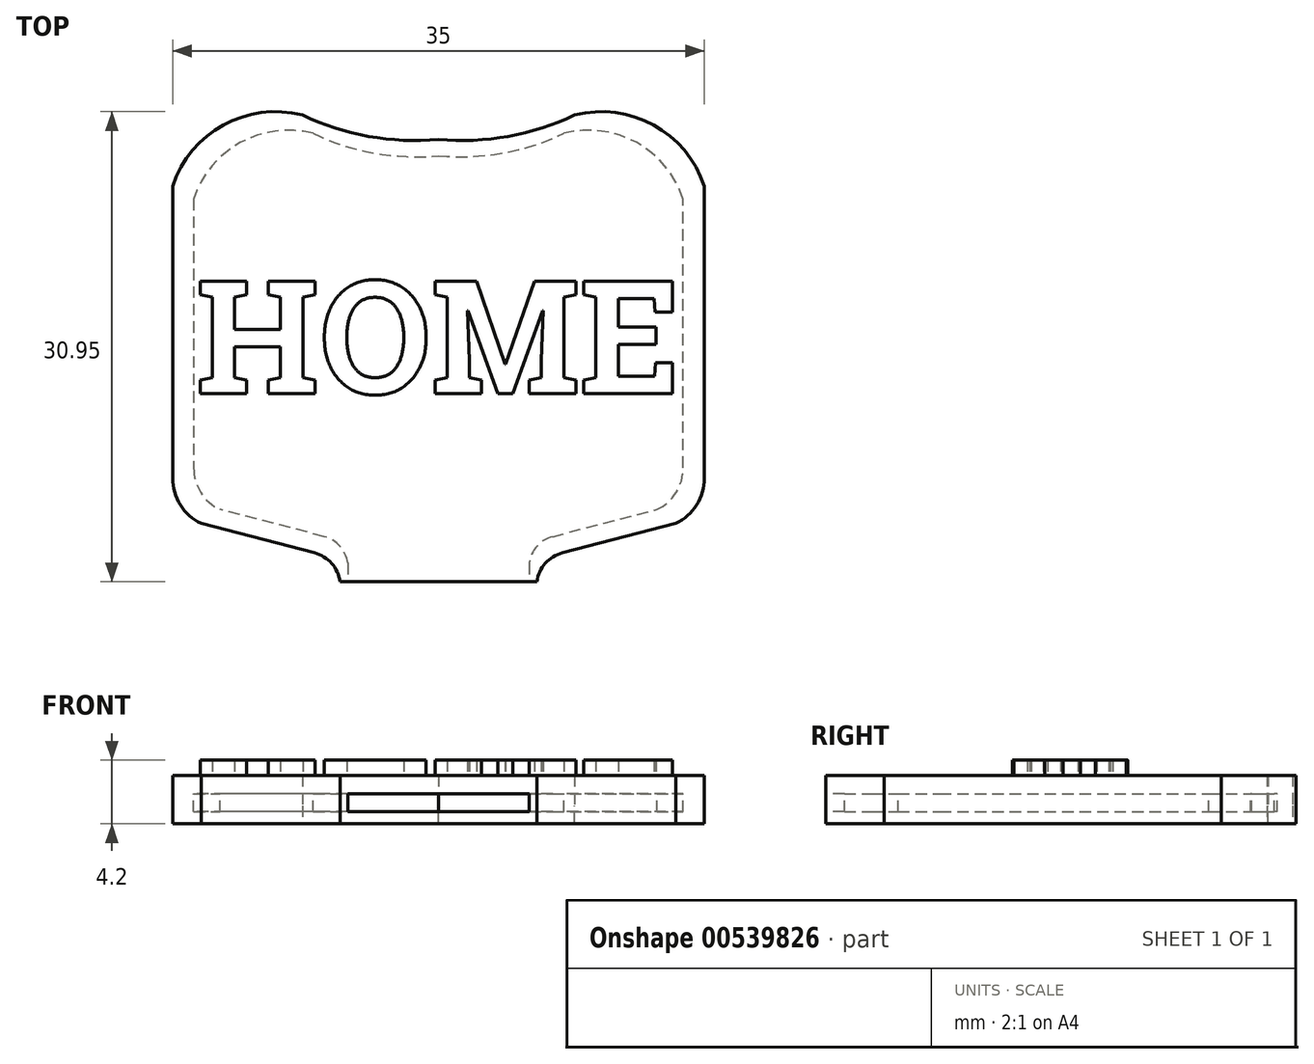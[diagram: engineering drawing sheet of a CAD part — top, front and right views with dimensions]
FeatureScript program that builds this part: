
annotation { "Feature Type Name" : "Feature", "Feature Type Description" : "" }
export const myFeature = defineFeature(function(context is Context, id is Id, definition is map)
    precondition{}
    {
        {
            var Q0;
            Q0=qCreatedBy(makeId("Top.planeOp"),FACE);
            var sketch = newSketch(context, id + "F0", { "sketchPlane" : qUnion([Q0])});
            skArc(sketch, "E0", {"start": v(-27.77, 71.26) * mm, "mid": v(-32.97, 70.6) * mm, "end": v(-36.3, 66.57) * mm});
            skLineSegment(sketch, "E1", {"start": v(-26.97, 42.44) * mm, "end": v(-34.42, 44.37) * mm});
            skArc(sketch, "E2", {"start": v(-36.3, 47.37) * mm, "mid": v(-35.8, 45.6) * mm, "end": v(-34.42, 44.37) * mm});
            skArc(sketch, "E3", {"start": v(-27.77, 71.26) * mm, "mid": v(-23.4, 69.86) * mm, "end": v(-18.8, 69.66) * mm});
            skArc(sketch, "E4", {"start": v(-25.3, 40.54) * mm, "mid": v(-25.85, 41.75) * mm, "end": v(-26.97, 42.44) * mm});
            skArc(sketch, "E5.MirrorCS", {"start": v(-9.85, 71.26) * mm, "mid": v(-14.22, 69.86) * mm, "end": v(-18.8, 69.66) * mm});
            skArc(sketch, "E6.MirrorCS", {"start": v(-9.85, 71.26) * mm, "mid": v(-4.65, 70.6) * mm, "end": v(-1.3, 66.57) * mm});
            skLineSegment(sketch, "E7.MirrorCS", {"start": v(-1.3, 47.37) * mm, "end": v(-1.3, 66.57) * mm});
            skLineSegment(sketch, "E8.MirrorCS", {"start": v(-10.65, 42.44) * mm, "end": v(-3.2, 44.37) * mm});
            skArc(sketch, "E9.MirrorCS", {"start": v(-1.3, 47.37) * mm, "mid": v(-1.82, 45.6) * mm, "end": v(-3.2, 44.37) * mm});
            skArc(sketch, "E10.MirrorCS", {"start": v(-12.32, 40.54) * mm, "mid": v(-11.77, 41.75) * mm, "end": v(-10.65, 42.44) * mm});
            skLineSegment(sketch, "E11", {"start": v(-36.3, 66.57) * mm, "end": v(-36.3, 47.37) * mm});
            skLineSegment(sketch, "E12", {"start": v(-25.3, 40.54) * mm, "end": v(-12.32, 40.54) * mm});
            skSolve(sketch);
        }
        {
            var Q0;
            Q0 = qSketchRegion(id + "F0", true);
            extrude(context, id + "F1", {"entities" : qUnion([Q0]), "depth" : 1.2 * mm, "offsetDistance" : 25.4 * mm});
        }
        {
            var Q0;
            Q0=qCreatedBy(makeId("Top.planeOp"),FACE);
            var sketch = newSketch(context, id + "F2", { "sketchPlane" : qUnion([Q0])});
            skArc(sketch, "E13", {"start": v(-27.77, 71.26) * mm, "mid": v(-32.97, 70.6) * mm, "end": v(-36.3, 66.57) * mm});
            skLineSegment(sketch, "E14", {"start": v(-26.97, 42.44) * mm, "end": v(-34.43, 44.37) * mm});
            skArc(sketch, "E15", {"start": v(-36.3, 47.36) * mm, "mid": v(-35.8, 45.6) * mm, "end": v(-34.43, 44.37) * mm});
            skArc(sketch, "E16", {"start": v(-27.77, 71.26) * mm, "mid": v(-23.4, 69.86) * mm, "end": v(-18.8, 69.66) * mm});
            skArc(sketch, "E17", {"start": v(-25.3, 40.54) * mm, "mid": v(-25.85, 41.75) * mm, "end": v(-26.97, 42.44) * mm});
            skArc(sketch, "E18.MirrorCS", {"start": v(-9.85, 71.26) * mm, "mid": v(-14.22, 69.86) * mm, "end": v(-18.8, 69.66) * mm});
            skArc(sketch, "E19.MirrorCS", {"start": v(-9.85, 71.26) * mm, "mid": v(-4.65, 70.6) * mm, "end": v(-1.3, 66.57) * mm});
            skLineSegment(sketch, "E20.MirrorCS", {"start": v(-1.3, 47.36) * mm, "end": v(-1.3, 66.57) * mm});
            skLineSegment(sketch, "E21.MirrorCS", {"start": v(-10.65, 42.44) * mm, "end": v(-3.2, 44.37) * mm});
            skArc(sketch, "E22.MirrorCS", {"start": v(-1.3, 47.36) * mm, "mid": v(-1.82, 45.6) * mm, "end": v(-3.2, 44.37) * mm});
            skArc(sketch, "E23.MirrorCS", {"start": v(-12.32, 40.54) * mm, "mid": v(-11.77, 41.75) * mm, "end": v(-10.65, 42.44) * mm});
            skLineSegment(sketch, "E24", {"start": v(-36.3, 66.57) * mm, "end": v(-36.3, 47.36) * mm});
            skArc(sketch, "E25", {"start": v(-27.06, 70.05) * mm, "mid": v(-31.85, 69.45) * mm, "end": v(-34.92, 65.73) * mm});
            skLineSegment(sketch, "E26", {"start": v(-26.33, 43.5) * mm, "end": v(-33.19, 45.3) * mm});
            skArc(sketch, "E27", {"start": v(-34.92, 48.05) * mm, "mid": v(-34.45, 46.42) * mm, "end": v(-33.19, 45.3) * mm});
            skArc(sketch, "E28", {"start": v(-27.06, 70.05) * mm, "mid": v(-23.03, 68.76) * mm, "end": v(-18.8, 68.58) * mm});
            skArc(sketch, "E29", {"start": v(-24.78, 41.77) * mm, "mid": v(-25.29, 42.87) * mm, "end": v(-26.33, 43.5) * mm});
            skArc(sketch, "E30.MirrorCS", {"start": v(-10.56, 70.05) * mm, "mid": v(-14.58, 68.76) * mm, "end": v(-18.8, 68.58) * mm});
            skArc(sketch, "E31.MirrorCS", {"start": v(-10.56, 70.05) * mm, "mid": v(-5.77, 69.45) * mm, "end": v(-2.7, 65.73) * mm});
            skLineSegment(sketch, "E32.MirrorCS", {"start": v(-2.7, 48.05) * mm, "end": v(-2.7, 65.73) * mm});
            skLineSegment(sketch, "E33.MirrorCS", {"start": v(-11.3, 43.5) * mm, "end": v(-4.43, 45.3) * mm});
            skArc(sketch, "E34.MirrorCS", {"start": v(-2.7, 48.05) * mm, "mid": v(-3.16, 46.42) * mm, "end": v(-4.43, 45.3) * mm});
            skArc(sketch, "E35.MirrorCS", {"start": v(-12.84, 41.77) * mm, "mid": v(-12.33, 42.87) * mm, "end": v(-11.3, 43.5) * mm});
            skLineSegment(sketch, "E36", {"start": v(-34.92, 65.73) * mm, "end": v(-34.92, 48.05) * mm});
            skLineSegment(sketch, "E37", {"start": v(-25.3, 40.54) * mm, "end": v(-12.32, 40.54) * mm});
            skSolve(sketch);
        }
        {
            var Q0;
            Q0 = qSketchRegion(id + "F2", true);
            extrude(context, id + "F3", {"entities" : qUnion([Q0]), "operationType" : NewBodyOperationType.ADD, "depth" : 2 * mm, "offsetDistance" : 25.4 * mm});
        }
        {
            var Q0;
            Q0=makeQuery(id+"F3.opExtrude","CAP_FACE",FACE,{"disambiguationData":[OSD([sQuery(id+"F2.wireOp",EDGE,"E13"),sQuery(id+"F2.wireOp",EDGE,"E14"),sQuery(id+"F2.wireOp",EDGE,"E15"),sQuery(id+"F2.wireOp",EDGE,"E16"),sQuery(id+"F2.wireOp",EDGE,"E17"),sQuery(id+"F2.wireOp",EDGE,"E18.MirrorCS"),sQuery(id+"F2.wireOp",EDGE,"E19.MirrorCS"),sQuery(id+"F2.wireOp",EDGE,"E20.MirrorCS"),sQuery(id+"F2.wireOp",EDGE,"E21.MirrorCS"),sQuery(id+"F2.wireOp",EDGE,"E22.MirrorCS"),sQuery(id+"F2.wireOp",EDGE,"E23.MirrorCS"),sQuery(id+"F2.wireOp",EDGE,"E24"),sQuery(id+"F2.wireOp",EDGE,"E37")])],"isStart":false});
            var sketch = newSketch(context, id + "F4", { "sketchPlane" : qUnion([Q0])});
            skArc(sketch, "E38", {"start": v(-27.06, 70.06) * mm, "mid": v(-31.85, 69.45) * mm, "end": v(-34.92, 65.74) * mm});
            skLineSegment(sketch, "E39", {"start": v(-26.33, 43.51) * mm, "end": v(-33.19, 45.3) * mm});
            skArc(sketch, "E40", {"start": v(-34.92, 48.05) * mm, "mid": v(-34.45, 46.42) * mm, "end": v(-33.19, 45.3) * mm});
            skArc(sketch, "E41", {"start": v(-27.06, 70.06) * mm, "mid": v(-23.04, 68.77) * mm, "end": v(-18.8, 68.58) * mm});
            skArc(sketch, "E42", {"start": v(-24.78, 41.77) * mm, "mid": v(-25.29, 42.87) * mm, "end": v(-26.33, 43.51) * mm});
            skArc(sketch, "E43.MirrorCS", {"start": v(-10.56, 70.06) * mm, "mid": v(-14.58, 68.77) * mm, "end": v(-18.8, 68.58) * mm});
            skArc(sketch, "E44.MirrorCS", {"start": v(-10.56, 70.06) * mm, "mid": v(-5.77, 69.45) * mm, "end": v(-2.7, 65.74) * mm});
            skLineSegment(sketch, "E45.MirrorCS", {"start": v(-2.7, 48.05) * mm, "end": v(-2.7, 65.74) * mm});
            skLineSegment(sketch, "E46.MirrorCS", {"start": v(-11.3, 43.51) * mm, "end": v(-4.43, 45.3) * mm});
            skArc(sketch, "E47.MirrorCS", {"start": v(-2.7, 48.05) * mm, "mid": v(-3.16, 46.42) * mm, "end": v(-4.43, 45.3) * mm});
            skArc(sketch, "E48.MirrorCS", {"start": v(-12.84, 41.77) * mm, "mid": v(-12.33, 42.87) * mm, "end": v(-11.3, 43.51) * mm});
            skLineSegment(sketch, "E49", {"start": v(-34.92, 65.74) * mm, "end": v(-34.92, 48.05) * mm});
            skLineSegment(sketch, "E50", {"start": v(-24.78, 41.77) * mm, "end": v(-24.78, 40.54) * mm});
            skLineSegment(sketch, "E51", {"start": v(-12.84, 41.77) * mm, "end": v(-12.84, 40.54) * mm});
            skLineSegment(sketch, "E52", {"start": v(-12.84, 40.54) * mm, "end": v(-24.78, 40.54) * mm});
            skSolve(sketch);
        }
        {
            var Q0;
            Q0 = qSketchRegion(id + "F4", true);
            extrude(context, id + "F5", {"entities" : qUnion([Q0]), "operationType" : NewBodyOperationType.REMOVE, "oppositeDirection" : true, "depth" : 1.2 * mm, "offsetDistance" : 25.4 * mm});
        }
        {
            var Q0;
            Q0=makeQuery(id+"F3.opExtrude","CAP_FACE",FACE,{"disambiguationData":[OSD([sQuery(id+"F2.wireOp",EDGE,"E13"),sQuery(id+"F2.wireOp",EDGE,"E14"),sQuery(id+"F2.wireOp",EDGE,"E15"),sQuery(id+"F2.wireOp",EDGE,"E16"),sQuery(id+"F2.wireOp",EDGE,"E17"),sQuery(id+"F2.wireOp",EDGE,"E18.MirrorCS"),sQuery(id+"F2.wireOp",EDGE,"E19.MirrorCS"),sQuery(id+"F2.wireOp",EDGE,"E20.MirrorCS"),sQuery(id+"F2.wireOp",EDGE,"E21.MirrorCS"),sQuery(id+"F2.wireOp",EDGE,"E22.MirrorCS"),sQuery(id+"F2.wireOp",EDGE,"E23.MirrorCS"),sQuery(id+"F2.wireOp",EDGE,"E24"),sQuery(id+"F2.wireOp",EDGE,"E37")])],"isStart":false});
            var sketch = newSketch(context, id + "F6", { "sketchPlane" : qUnion([Q0])});
            skArc(sketch, "E53", {"start": v(-27.77, 71.26) * mm, "mid": v(-32.97, 70.6) * mm, "end": v(-36.3, 66.57) * mm});
            skLineSegment(sketch, "E54", {"start": v(-26.97, 42.44) * mm, "end": v(-34.43, 44.37) * mm});
            skArc(sketch, "E55", {"start": v(-36.3, 47.36) * mm, "mid": v(-35.8, 45.6) * mm, "end": v(-34.43, 44.37) * mm});
            skArc(sketch, "E56", {"start": v(-27.77, 71.26) * mm, "mid": v(-23.4, 69.86) * mm, "end": v(-18.8, 69.66) * mm});
            skArc(sketch, "E57", {"start": v(-25.3, 40.54) * mm, "mid": v(-25.85, 41.75) * mm, "end": v(-26.97, 42.44) * mm});
            skArc(sketch, "E58.MirrorCS", {"start": v(-9.85, 71.26) * mm, "mid": v(-14.22, 69.86) * mm, "end": v(-18.8, 69.66) * mm});
            skArc(sketch, "E59.MirrorCS", {"start": v(-9.85, 71.26) * mm, "mid": v(-4.65, 70.6) * mm, "end": v(-1.3, 66.57) * mm});
            skLineSegment(sketch, "E60.MirrorCS", {"start": v(-1.3, 47.36) * mm, "end": v(-1.3, 66.57) * mm});
            skLineSegment(sketch, "E61.MirrorCS", {"start": v(-10.65, 42.44) * mm, "end": v(-3.2, 44.37) * mm});
            skArc(sketch, "E62.MirrorCS", {"start": v(-1.3, 47.36) * mm, "mid": v(-1.82, 45.6) * mm, "end": v(-3.2, 44.37) * mm});
            skArc(sketch, "E63.MirrorCS", {"start": v(-12.32, 40.54) * mm, "mid": v(-11.77, 41.75) * mm, "end": v(-10.65, 42.44) * mm});
            skLineSegment(sketch, "E64", {"start": v(-36.3, 66.57) * mm, "end": v(-36.3, 47.36) * mm});
            skLineSegment(sketch, "E65", {"start": v(-25.3, 40.54) * mm, "end": v(-12.32, 40.54) * mm});
            skSolve(sketch);
        }
        {
            var Q0;
            Q0 = qSketchRegion(id + "F6", true);
            extrude(context, id + "F7", {"entities" : qUnion([Q0]), "operationType" : NewBodyOperationType.ADD, "depth" : 1.2 * mm, "offsetDistance" : 25.4 * mm});
        }
        {
            var Q0;
            Q0=makeQuery(id+"F7.opExtrude","CAP_FACE",FACE,{"disambiguationData":[OSD([sQuery(id+"F6.wireOp",EDGE,"E53"),sQuery(id+"F6.wireOp",EDGE,"E54"),sQuery(id+"F6.wireOp",EDGE,"E55"),sQuery(id+"F6.wireOp",EDGE,"E56"),sQuery(id+"F6.wireOp",EDGE,"E57"),sQuery(id+"F6.wireOp",EDGE,"E58.MirrorCS"),sQuery(id+"F6.wireOp",EDGE,"E59.MirrorCS"),sQuery(id+"F6.wireOp",EDGE,"E60.MirrorCS"),sQuery(id+"F6.wireOp",EDGE,"E61.MirrorCS"),sQuery(id+"F6.wireOp",EDGE,"E62.MirrorCS"),sQuery(id+"F6.wireOp",EDGE,"E63.MirrorCS"),sQuery(id+"F6.wireOp",EDGE,"E64"),sQuery(id+"F6.wireOp",EDGE,"E65")])],"isStart":false});
            var sketch = newSketch(context, id + "F8", { "sketchPlane" : qUnion([Q0])});
            skText(sketch, "E66", { "text": "HOME", "fontName": "RobotoSlab-Bold.ttf"});
            const initialGuessF8  = {"E66": [-0.03478, 0.05293, 1, 0, 0.00748]};
            skSetInitialGuess(sketch, initialGuessF8);
            skSolve(sketch);
        }
        {
            var Q0;
            Q0 = qSketchRegion(id + "F8", true);
            extrude(context, id + "F9", {"entities" : qUnion([Q0]), "operationType" : NewBodyOperationType.ADD, "depth" : 1 * mm, "offsetDistance" : 25.4 * mm});
        }
    });
